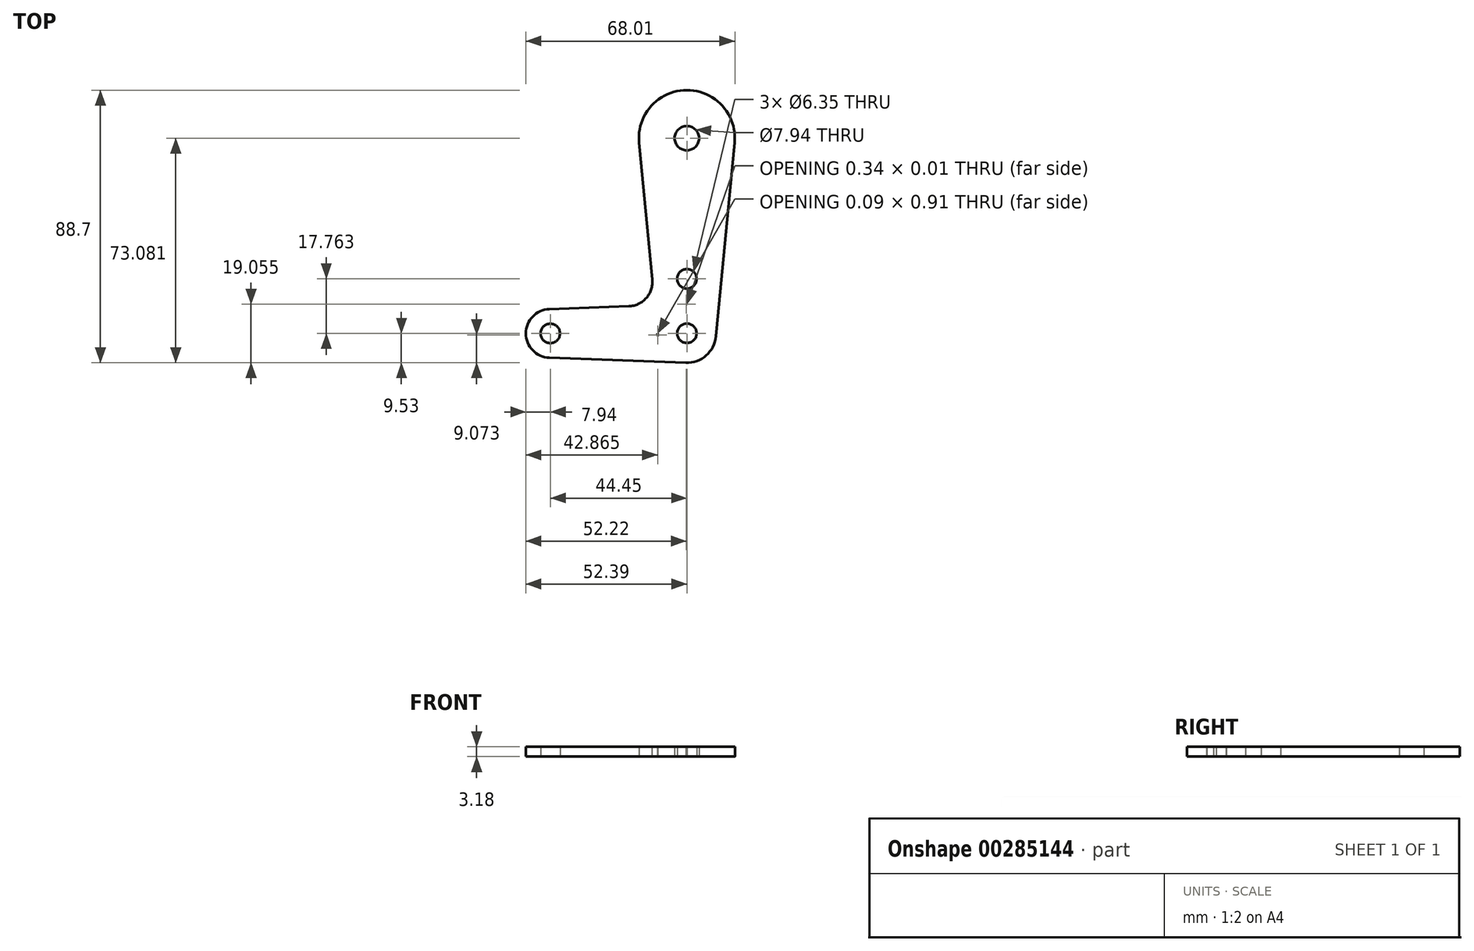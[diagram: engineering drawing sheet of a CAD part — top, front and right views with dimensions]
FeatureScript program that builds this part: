
annotation { "Feature Type Name" : "Feature", "Feature Type Description" : "" }
export const myFeature = defineFeature(function(context is Context, id is Id, definition is map)
    precondition{}
    {
        {
            var Q0;
            Q0=qCreatedBy(makeId("Top.planeOp"),FACE);
            var sketch = newSketch(context, id + "F0", { "sketchPlane" : qUnion([Q0])});
            skCircle(sketch, "E0", {"center": v(0, 0) * mm, "radius": 9.53 * mm});
            skLineSegment(sketch, "E1", {"start": v(0, 0) * mm, "end": v(-44.45, 0) * mm});
            skLineSegment(sketch, "E2", {"start": v(0, 0.05) * mm, "end": v(0, 63.55) * mm});
            skCircle(sketch, "E3", {"center": v(-44.45, 0) * mm, "radius": 3.18 * mm});
            skCircle(sketch, "E4", {"center": v(0, 63.55) * mm, "radius": 3.97 * mm});
            skCircle(sketch, "E5", {"center": v(0, 17.76) * mm, "radius": 3.18 * mm});
            skCircle(sketch, "E6", {"center": v(0, 63.55) * mm, "radius": 15.62 * mm});
            skCircle(sketch, "E7", {"center": v(0, 0.05) * mm, "radius": 3.18 * mm});
            skCircle(sketch, "E8", {"center": v(-44.45, 0) * mm, "radius": 7.94 * mm});
            skLineSegment(sketch, "E9", {"start": v(-44.73, 7.93) * mm, "end": v(0, 9.53) * mm});
            skLineSegment(sketch, "E10", {"start": v(-44.73, -7.93) * mm, "end": v(-0.34, -9.52) * mm});
            skLineSegment(sketch, "E11", {"start": v(9.48, -0.91) * mm, "end": v(15.55, 62.05) * mm});
            skLineSegment(sketch, "E12", {"start": v(-9.48, -0.91) * mm, "end": v(-15.55, 62.05) * mm});
            skSolve(sketch);
        }
        {
            var Q0;
            Q0=makeQuery(id+"F0.imprint","IMPRINT",FACE,{"disambiguationData":[TD([[makeQuery(id+"F0.imprint","IMPRINT",EDGE,{"derivedFrom":sQuery(id+"F0.wireOp",EDGE,"E4")}),-1.0]])]});
            var Q1;
            {var subQ3=sQuery(id+"F0.wireOp",EDGE,"E2");var subQ8=sQuery(id+"F0.wireOp",EDGE,"E9");var subQ11=makeQuery(id+"F0.imprint","INTERSECT",VERTEX,{"derivedFrom":[subQ3,subQ8]});Q1=makeQuery(id+"F0.imprint","IMPRINT",FACE,{"disambiguationData":[TD([[makeQuery(id+"F0.imprint","IMPRINT",EDGE,{"disambiguationData":[TD([[subQ11,-1.0]])],"derivedFrom":subQ3}),1.0]])]});}
            var Q2;
            {var subQ9=sQuery(id+"F0.wireOp",EDGE,"E11");Q2=makeQuery(id+"F0.imprint","IMPRINT",FACE,{"disambiguationData":[TD([[makeQuery(id+"F0.imprint","IMPRINT",EDGE,{"derivedFrom":subQ9}),1.0]])]});}
            var Q3;
            {var subQ0=sQuery(id+"F0.wireOp",EDGE,"E8");var subQ1=sQuery(id+"F0.wireOp",EDGE,"E1");var subQ2=makeQuery(id+"F0.imprint","INTERSECT",VERTEX,{"derivedFrom":[subQ1,subQ0]});Q3=makeQuery(id+"F0.imprint","IMPRINT",FACE,{"disambiguationData":[TD([[makeQuery(id+"F0.imprint","IMPRINT",EDGE,{"disambiguationData":[TD([[subQ2,1.0]])],"derivedFrom":subQ1}),-1.0]])]});}
            var Q4;
            {var subQ0=sQuery(id+"F0.wireOp",EDGE,"E10");Q4=makeQuery(id+"F0.imprint","IMPRINT",FACE,{"disambiguationData":[TD([[makeQuery(id+"F0.imprint","IMPRINT",EDGE,{"derivedFrom":subQ0}),1.0]])]});}
            var Q5;
            Q5=makeQuery(id+"F0.imprint","IMPRINT",FACE,{"disambiguationData":[TD([[makeQuery(id+"F0.imprint","IMPRINT",EDGE,{"derivedFrom":sQuery(id+"F0.wireOp",EDGE,"E3")}),-1.0]])]});
            var Q6;
            {var subQ0=sQuery(id+"F0.wireOp",EDGE,"E0");var subQ5=makeQuery(id+"F0.imprint","INTERSECT",VERTEX,{"derivedFrom":[subQ0,sQuery(id+"F0.wireOp",EDGE,"E12")]});Q6=makeQuery(id+"F0.imprint","IMPRINT",FACE,{"disambiguationData":[TD([[makeQuery(id+"F0.imprint","IMPRINT",EDGE,{"disambiguationData":[TD([[subQ5,1.0]])],"derivedFrom":subQ0}),1.0]])]});}
            var Q7;
            {var subQ3=sQuery(id+"F0.wireOp",EDGE,"E0");var subQ8=makeQuery(id+"F0.imprint","INTERSECT",VERTEX,{"derivedFrom":[subQ3,sQuery(id+"F0.wireOp",EDGE,"E9")]});Q7=makeQuery(id+"F0.imprint","IMPRINT",FACE,{"disambiguationData":[TD([[makeQuery(id+"F0.imprint","IMPRINT",EDGE,{"disambiguationData":[TD([[subQ8,1.0]])],"derivedFrom":subQ3}),1.0]])]});}
            var Q8;
            {var subQ0=sQuery(id+"F0.wireOp",EDGE,"E9");var subQ1=sQuery(id+"F0.wireOp",EDGE,"E0");var subQ2=makeQuery(id+"F0.imprint","INTERSECT",VERTEX,{"derivedFrom":[subQ1,subQ0]});Q8=makeQuery(id+"F0.imprint","IMPRINT",FACE,{"disambiguationData":[TD([[makeQuery(id+"F0.imprint","IMPRINT",EDGE,{"disambiguationData":[TD([[subQ2,-1.0]])],"derivedFrom":subQ1}),-1.0]])]});}
            extrude(context, id + "F1", {"entities" : qUnion([Q0, Q1, Q2, Q3, Q4, Q5, Q6, Q7, Q8]), "depth" : 3.17 * mm});
        }
        {
            var Q0;
            Q0=makeQuery(id+"F1.opExtrude","SWEPT_EDGE",EDGE,{"disambiguationData":[OSD([sQuery(id+"F0.wireOp",EDGE,"E9"),sQuery(id+"F0.wireOp",EDGE,"E12")])]});
            fillet(context, id + "F2", {"entities" : qUnion([Q0]), "radius" : 7.94 * mm, "tangentPropagation" : true, "allowEdgeOverflow" : false});
        }
    });
